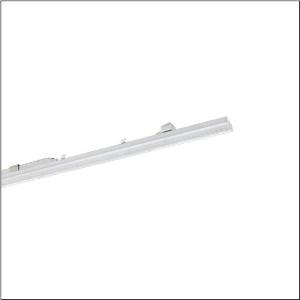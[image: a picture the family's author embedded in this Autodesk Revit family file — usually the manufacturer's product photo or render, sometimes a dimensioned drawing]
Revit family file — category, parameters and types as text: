
# Revit family: tl_l_5wd7a8f0b2c5
name_source: partatom
category: Lighting Fixtures
units: mm (PartAtom-declared; Revit-internal decimal feet)

## family parameters
Cut with Voids When Loaded = No
Host = Face
Light Source = No
Part Type = Normal
Room Calculation Point = No
Round Connector Dimension = Use Diameter
Shared = No

## types (1)
- TL L (1 x LED, 9800 lm, 63.3 W, 4000K)
    Apparent Load = 63 VA
    CIE Flux Codes = 49 84 98 100 100
    Color Rendering = 80
    Color Temperature = 4000K
    Default Elevation = 1800 mm
    Description = TL L, luminaire insert, of sheet steel, galvanised, coil coated, white, length: 1.500mm, width: 66mm, height: 67mm, micro fuse,LED rated luminous flux: 9.800lm, light colour: 840, control gear: 4..20mA, with terminal, 5-pole, mains connection: 230..240V, AC, 50/60Hz, rated input power: 63W, primary optical cover: cover, of PMMA, light emission: direct distribution, protection rating (complete): as luminaire, insulation class (complete): insulation class I (protective earthing), certification: CE, impact resistance: IK06, permissible ambient temperature for indoor applications: -25..+35°C, packaging unit: 1 piece
    Height = 120 mm
    Lamp = 1 x LED
    Lamp Light Flux = 9800 lm
    Lamp Power = 63.3 W
    Lamp count = 1
    Length = 1690 mm
    Luminous efficacy = 155 lm/W
    Manufacturer = Siteco
    ModVariant = No
    Model = 5WD7A8F0B2C5
    Mounting Place = Ceiling
    Mounting Type = Pendant
    Number of Poles = 1
    OnlyDefault = Yes
    Power Factor = 1
    Product Name = TL L
    Product group = luminaire insert
    ProductGroupID = 901
    Protection Class = Protection class I
    Protection Degree = Degree of protection
    RLX_Detail_Level = 1
    RLX_Emergency_Light_Flux = 0 lm
    RLX_Emergency_Type = 0
    RLX_Emergency_Type_DB = No
    RlxData = <blob elided: 14137 chars, md5=d6a281bd>
    Socket = socket
    Standby Power = 0 W
    System Light Flux = 9800 lm
    System Power = 63 W
    Type Comments = Product without accessories
    Type Image = l_1294382.jpg
    URL = http://relux.com
    VarID = ---
    Voltage = 0 V
    Weight = 0.00 kg
    Width = 208 mm

## geometry (parser evidence)
native form markers: Sweep x12
no freeform markers — native parametric forms only
